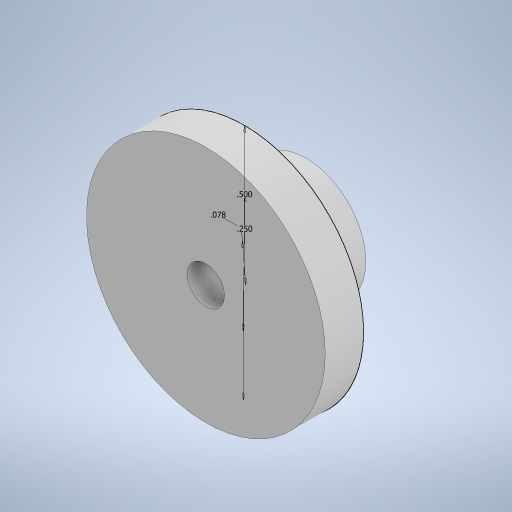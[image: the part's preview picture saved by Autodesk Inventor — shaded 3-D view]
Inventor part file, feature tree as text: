
AUTODESK INVENTOR PART (.ipt)
format: ipt  version: 2023 (Build 270158000, 158)  size: 237,568 bytes
history: native  units: in
note: dims shown in document units (in); Inventor stores cm internally (conversion verified against a paired STEP export)
features: extrude x3, sketch x2
ambient origin geometry x8: Origin, YZ Plane, XZ Plane, XY Plane, X Axis, Y Axis, Z Axis, Center Point
bodies: Solid1 (feature_tree)
feature tree (5):
  sketch  "Sketch1"  dims[d0=0.5in d1=0.25in]
  extrude  "Extrusion1"  Depth=0.25in
  extrude  "Extrusion2"  Depth=0.13in TaperAngle=0.0deg
  extrude  "Extrusion3"  Depth=0.13in TaperAngle=0.0deg
  sketch  "Sketch2"  dims[d2=0.0781in d3=0.08in d4=0.0in d5=0.13in d6=0.0in d7=0.056in d8=0.065in d9=0.13in d10=0.0in]
